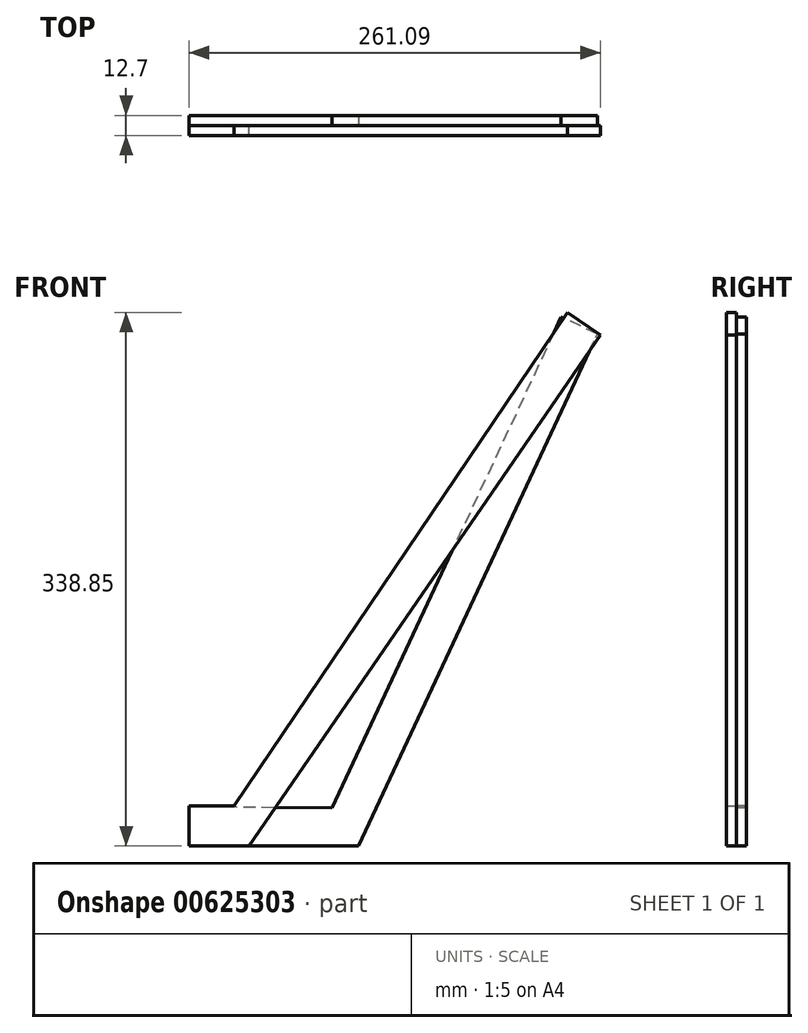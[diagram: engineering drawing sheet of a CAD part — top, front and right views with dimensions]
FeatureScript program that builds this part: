
annotation { "Feature Type Name" : "Feature", "Feature Type Description" : "" }
export const myFeature = defineFeature(function(context is Context, id is Id, definition is map)
    precondition{}
    {
        {
            var Q0;
            Q0=qCreatedBy(makeId("Front.planeOp"),FACE);
            var sketch = newSketch(context, id + "F0", { "sketchPlane" : qUnion([Q0])});
            skLineSegment(sketch, "E0", {"start": v(0, 0) * mm, "end": v(38.1, 0) * mm});
            skLineSegment(sketch, "E1", {"start": v(0, 0) * mm, "end": v(0, 25.4) * mm});
            skLineSegment(sketch, "E2", {"start": v(0, 25.4) * mm, "end": v(28.58, 25.4) * mm});
            skLineSegment(sketch, "E3", {"start": v(28.58, 25.4) * mm, "end": v(38.1, 0) * mm});
            skLineSegment(sketch, "E4", {"start": v(28.58, 0) * mm, "end": v(28.58, 25.4) * mm});
            skLineSegment(sketch, "E5", {"start": v(28.58, 25.4) * mm, "end": v(47.2, 8.13) * mm});
            skLineSegment(sketch, "E6", {"start": v(38.1, 0) * mm, "end": v(261.1, 324.46) * mm});
            skLineSegment(sketch, "E7", {"start": v(261.1, 324.46) * mm, "end": v(240.16, 338.85) * mm});
            skLineSegment(sketch, "E8", {"start": v(240.16, 338.85) * mm, "end": v(28.57, 25.4) * mm});
            skLineSegment(sketch, "E9", {"start": v(28.58, 0) * mm, "end": v(0, 0) * mm});
            skLineSegment(sketch, "E10", {"start": v(0, 25.4) * mm, "end": v(55.56, 25.4) * mm});
            skPoint(sketch, "E11.orphan", {"position": v(107.58, 0) * mm});
            skSolve(sketch);
        }
        {
            var Q0;
            Q0 = qSketchRegion(id + "F0", true);
            extrude(context, id + "F1", {"entities" : qUnion([Q0]), "depth" : 6.35 * mm, "offsetDistance" : 25.4 * mm});
        }
        {
            var Q0;
            Q0=qCreatedBy(makeId("Front.planeOp"),FACE);
            var sketch = newSketch(context, id + "F2", { "sketchPlane" : qUnion([Q0])});
            skLineSegment(sketch, "E12", {"start": v(0, 0) * mm, "end": v(107.57, 0) * mm});
            skLineSegment(sketch, "E13", {"start": v(107.57, 0) * mm, "end": v(259.27, 325.32) * mm});
            skLineSegment(sketch, "E14", {"start": v(259.27, 325.32) * mm, "end": v(236.25, 336.06) * mm});
            skLineSegment(sketch, "E15", {"start": v(236.25, 336.06) * mm, "end": v(90.83, 24.2) * mm});
            skLineSegment(sketch, "E16", {"start": v(0, 0) * mm, "end": v(0, 25.4) * mm});
            skLineSegment(sketch, "E17", {"start": v(0, 25.4) * mm, "end": v(90.83, 24.2) * mm});
            skPoint(sketch, "E18.orphan", {"position": v(275.16, 21.76) * mm});
            skPoint(sketch, "E19.orphan", {"position": v(89.7, 21.76) * mm});
            skSolve(sketch);
        }
        {
            var Q0;
            Q0 = qSketchRegion(id + "F2", true);
            extrude(context, id + "F3", {"entities" : qUnion([Q0]), "oppositeDirection" : true, "depth" : 6.35 * mm, "offsetDistance" : 25.4 * mm});
        }
    });
